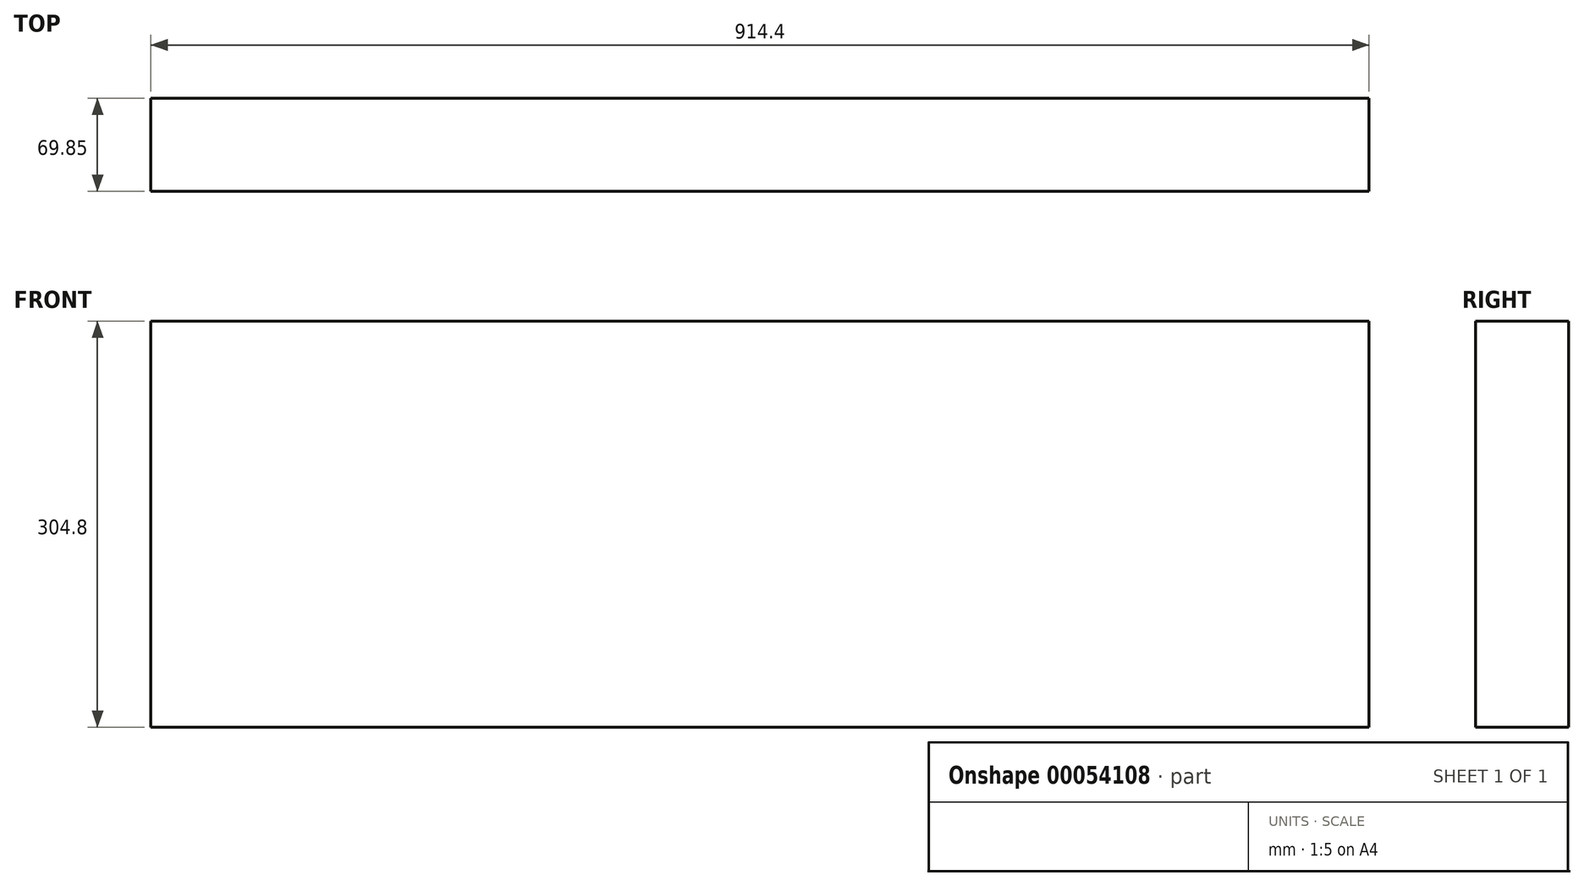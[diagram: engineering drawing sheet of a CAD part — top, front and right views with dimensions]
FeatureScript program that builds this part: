
annotation { "Feature Type Name" : "Feature", "Feature Type Description" : "" }
export const myFeature = defineFeature(function(context is Context, id is Id, definition is map)
    precondition{}
    {
        {
            var Q0;
            Q0=qCreatedBy(makeId("Top.planeOp"),FACE);
            var sketch = newSketch(context, id + "F0", { "sketchPlane" : qUnion([Q0])});
            skLineSegment(sketch, "E0.bottom", {"start": v(-464.77, -18.65) * mm, "end": v(449.63, -18.65) * mm});
            skLineSegment(sketch, "E0.top", {"start": v(-464.77, 51.2) * mm, "end": v(449.63, 51.2) * mm});
            skLineSegment(sketch, "E0.left", {"start": v(-464.77, -18.65) * mm, "end": v(-464.77, 51.2) * mm});
            skLineSegment(sketch, "E0.right", {"start": v(449.63, -18.65) * mm, "end": v(449.63, 51.2) * mm});
            skSolve(sketch);
        }
        {
            var Q0;
            Q0 = qSketchRegion(id + "F0", true);
            extrude(context, id + "F1", {"entities" : qUnion([Q0]), "depth" : 304.8 * mm});
        }
    });
